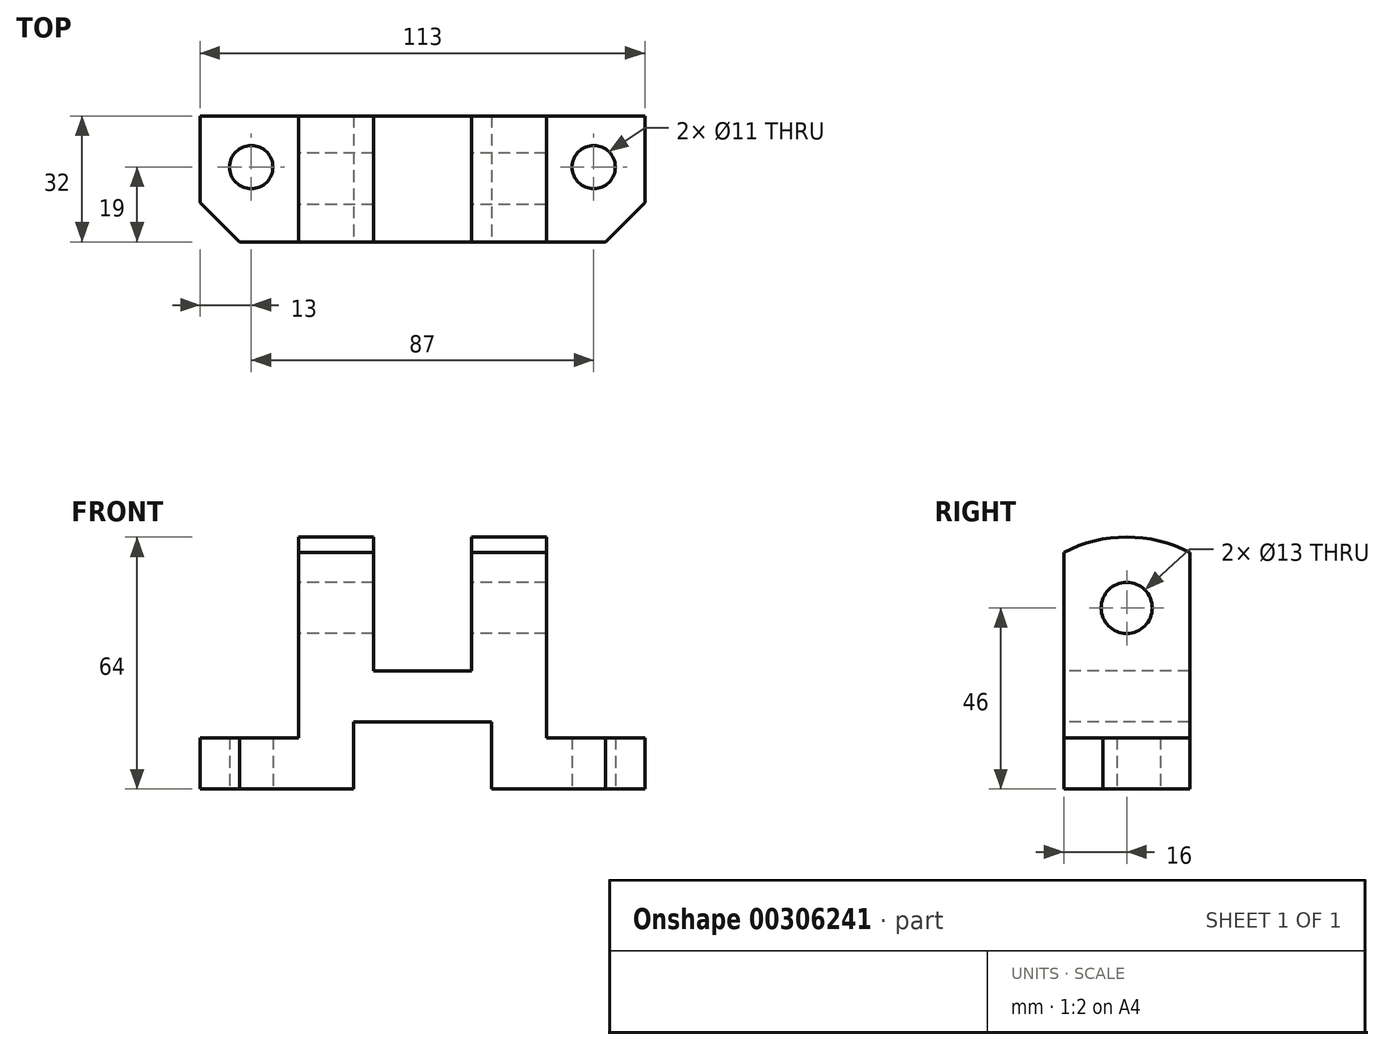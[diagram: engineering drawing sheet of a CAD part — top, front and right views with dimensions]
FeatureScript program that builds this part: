
annotation { "Feature Type Name" : "Feature", "Feature Type Description" : "" }
export const myFeature = defineFeature(function(context is Context, id is Id, definition is map)
    precondition{}
    {
        {
            var Q0;
            Q0=qCreatedBy(makeId("Front.planeOp"),FACE);
            var sketch = newSketch(context, id + "F0", { "sketchPlane" : qUnion([Q0])});
            skLineSegment(sketch, "E0", {"start": v(0, 0) * mm, "end": v(39, 0) * mm});
            skLineSegment(sketch, "E1", {"start": v(39, 0) * mm, "end": v(39, 17) * mm});
            skLineSegment(sketch, "E2", {"start": v(39, 17) * mm, "end": v(74, 17) * mm});
            skLineSegment(sketch, "E3", {"start": v(74, 17) * mm, "end": v(74, 0) * mm});
            skLineSegment(sketch, "E4", {"start": v(74, 0) * mm, "end": v(113, 0) * mm});
            skLineSegment(sketch, "E5", {"start": v(113, 0) * mm, "end": v(113, 13) * mm});
            skLineSegment(sketch, "E6", {"start": v(113, 13) * mm, "end": v(88, 13) * mm});
            skLineSegment(sketch, "E7", {"start": v(88, 13) * mm, "end": v(88, 64) * mm});
            skLineSegment(sketch, "E8", {"start": v(88, 64) * mm, "end": v(69, 64) * mm});
            skLineSegment(sketch, "E9", {"start": v(44, 64) * mm, "end": v(25, 64) * mm});
            skLineSegment(sketch, "E10", {"start": v(25, 64) * mm, "end": v(25, 13) * mm});
            skLineSegment(sketch, "E11", {"start": v(25, 13) * mm, "end": v(0, 13) * mm});
            skLineSegment(sketch, "E12", {"start": v(0, 13) * mm, "end": v(0, 0) * mm});
            skLineSegment(sketch, "E13", {"start": v(44, 64) * mm, "end": v(44, 30) * mm});
            skLineSegment(sketch, "E14", {"start": v(44, 30) * mm, "end": v(69, 30) * mm});
            skLineSegment(sketch, "E15", {"start": v(69, 30) * mm, "end": v(69, 64) * mm});
            skSolve(sketch);
        }
        {
            var Q0;
            Q0 = qSketchRegion(id + "F0", true);
            extrude(context, id + "F1", {"entities" : qUnion([Q0]), "oppositeDirection" : true, "depth" : 32 * mm});
        }
        {
            var Q0;
            Q0=qCreatedBy(makeId("Right.planeOp"),FACE);
            var sketch = newSketch(context, id + "F2", { "sketchPlane" : qUnion([Q0])});
            skLineSegment(sketch, "E16", {"start": v(0, 80.83) * mm, "end": v(32, 80.83) * mm});
            skLineSegment(sketch, "E17", {"start": v(32, 80.83) * mm, "end": v(32, 60.13) * mm});
            skLineSegment(sketch, "E18", {"start": v(0, 80.83) * mm, "end": v(0, 60.13) * mm});
            skArc(sketch, "E19", {"start": v(32, 60.13) * mm, "mid": v(16, 64) * mm, "end": v(0, 60.13) * mm});
            skCircle(sketch, "E20", {"center": v(16, 46) * mm, "radius": 6.5 * mm});
            skSolve(sketch);
        }
        {
            var Q0;
            Q0 = qSketchRegion(id + "F2", true);
            extrude(context, id + "F3", {"entities" : qUnion([Q0]), "operationType" : NewBodyOperationType.REMOVE, "endBound" : BoundingType.THROUGH_ALL, "depth" : 25 * mm});
        }
        {
            var Q0;
            Q0=qCreatedBy(makeId("Top.planeOp"),FACE);
            var sketch = newSketch(context, id + "F4", { "sketchPlane" : qUnion([Q0])});
            skCircle(sketch, "E21", {"center": v(13, 19) * mm, "radius": 5.5 * mm});
            skCircle(sketch, "E22", {"center": v(100, 19) * mm, "radius": 5.5 * mm});
            skLineSegment(sketch, "E23", {"start": v(0, 10) * mm, "end": v(10, 0) * mm});
            skLineSegment(sketch, "E24", {"start": v(10, 0) * mm, "end": v(0, 0) * mm});
            skLineSegment(sketch, "E25", {"start": v(0, 0) * mm, "end": v(0, 10) * mm});
            skLineSegment(sketch, "E26", {"start": v(113, 0) * mm, "end": v(113, 10) * mm});
            skLineSegment(sketch, "E27", {"start": v(113, 10) * mm, "end": v(103, 0) * mm});
            skLineSegment(sketch, "E28", {"start": v(103, 0) * mm, "end": v(113, 0) * mm});
            skSolve(sketch);
        }
        {
            var Q0;
            Q0 = qSketchRegion(id + "F4", true);
            extrude(context, id + "F5", {"entities" : qUnion([Q0]), "operationType" : NewBodyOperationType.REMOVE, "endBound" : BoundingType.THROUGH_ALL, "depth" : 25 * mm});
        }
    });
